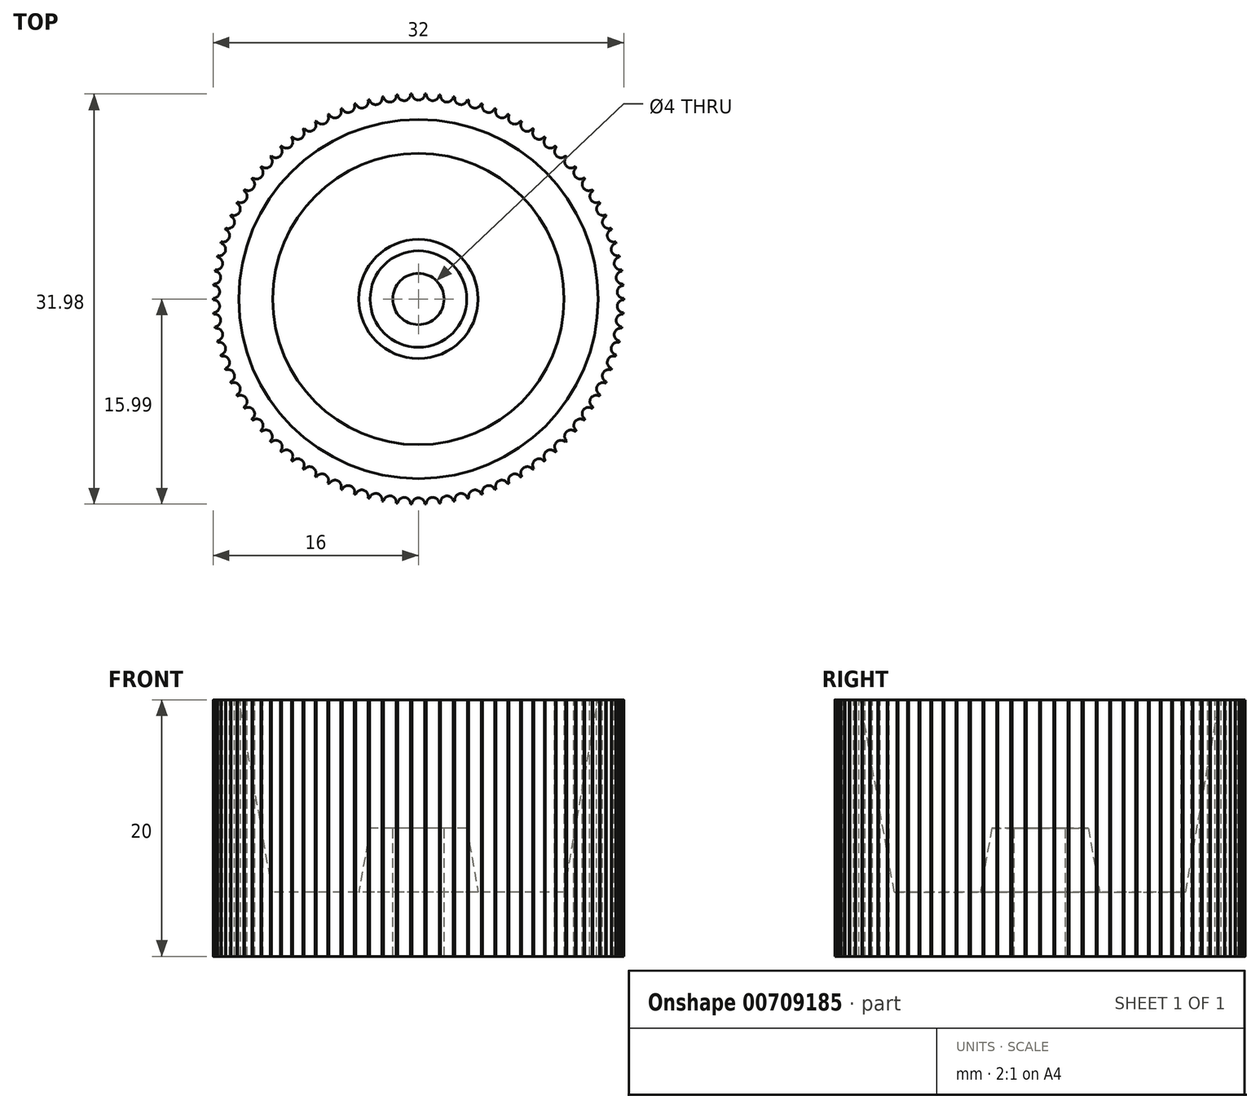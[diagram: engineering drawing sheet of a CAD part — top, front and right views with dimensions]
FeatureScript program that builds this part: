
annotation { "Feature Type Name" : "Feature", "Feature Type Description" : "" }
export const myFeature = defineFeature(function(context is Context, id is Id, definition is map)
    precondition{}
    {
        {
            var Q0;
            Q0=qCreatedBy(makeId("Top.planeOp"),FACE);
            var sketch = newSketch(context, id + "F0", { "sketchPlane" : qUnion([Q0])});
            skCircle(sketch, "E0", {"center": v(0, 0) * mm, "radius": 16 * mm});
            skCircle(sketch, "E1", {"center": v(0, 0) * mm, "radius": 14 * mm});
            skCircle(sketch, "E2", {"center": v(0, 0) * mm, "radius": 2 * mm});
            skCircle(sketch, "E3", {"center": v(0, 0) * mm, "radius": 6 * mm});
            skCircle(sketch, "E4", {"center": v(0, 16) * mm, "radius": 0.5 * mm});
            skSolve(sketch);
        }
        {
            var Q0;
            Q0=makeQuery(id+"F0.imprint","IMPRINT",FACE,{"disambiguationData":[TD([[makeQuery(id+"F0.imprint","IMPRINT",EDGE,{"derivedFrom":sQuery(id+"F0.wireOp",EDGE,"E0")}),1.0]])]});
            var Q1;
            Q1=makeQuery(id+"F0.imprint","IMPRINT",FACE,{"disambiguationData":[TD([[makeQuery(id+"F0.imprint","IMPRINT",EDGE,{"derivedFrom":sQuery(id+"F0.wireOp",EDGE,"E1")}),1.0]])]});
            var Q2;
            Q2=makeQuery(id+"F0.imprint","IMPRINT",FACE,{"disambiguationData":[TD([[makeQuery(id+"F0.imprint","IMPRINT",EDGE,{"derivedFrom":sQuery(id+"F0.wireOp",EDGE,"E2")}),-1.0]])]});
            var Q3;
            Q3=makeQuery(id+"F0.imprint","IMPRINT",FACE,{"disambiguationData":[TD([[makeQuery(id+"F0.imprint","IMPRINT",EDGE,{"derivedFrom":sQuery(id+"F0.wireOp",EDGE,"E1")}),-1.0]])]});
            extrude(context, id + "F1", {"entities" : qUnion([Q0, Q1, Q2, Q3]), "oppositeDirection" : true, "depth" : 20 * mm, "offsetDistance" : 25 * mm});
        }
        {
            var Q0;
            Q0=makeQuery(id+"F0.imprint","IMPRINT",FACE,{"disambiguationData":[TD([[makeQuery(id+"F0.imprint","IMPRINT",EDGE,{"derivedFrom":sQuery(id+"F0.wireOp",EDGE,"E1")}),1.0]])]});
            var Q1;
            Q1=makeQuery(id+"F0.imprint","IMPRINT",FACE,{"disambiguationData":[TD([[makeQuery(id+"F0.imprint","IMPRINT",EDGE,{"derivedFrom":sQuery(id+"F0.wireOp",EDGE,"E2")}),-1.0]])]});
            extrude(context, id + "F2", {"entities" : qUnion([Q0, Q1]), "operationType" : NewBodyOperationType.REMOVE, "oppositeDirection" : true, "depth" : 15 * mm, "offsetDistance" : 25 * mm, "hasDraft" : true, "draftAngle" : 10 * degree, "draftPullDirection" : true});
        }
        {
            var Q0;
            Q0=makeQuery(id+"F0.imprint","IMPRINT",FACE,{"disambiguationData":[TD([[makeQuery(id+"F0.imprint","IMPRINT",EDGE,{"derivedFrom":sQuery(id+"F0.wireOp",EDGE,"E2")}),-1.0]])]});
            extrude(context, id + "F3", {"entities" : qUnion([Q0]), "operationType" : NewBodyOperationType.REMOVE, "oppositeDirection" : true, "depth" : 10 * mm, "offsetDistance" : 25 * mm});
        }
        {
            var Q0;
            {var subQ0=sQuery(id+"F0.wireOp",EDGE,"E4");var subQ1=sQuery(id+"F0.wireOp",EDGE,"E0");var subQ2=makeQuery(id+"F0.imprint","INTERSECT",VERTEX,{"disambiguationData":[OD(0.0)],"derivedFrom":[subQ1,subQ0]});Q0=makeQuery(id+"F0.imprint","IMPRINT",FACE,{"disambiguationData":[TD([[makeQuery(id+"F0.imprint","IMPRINT",EDGE,{"disambiguationData":[TD([[subQ2,1.0]])],"derivedFrom":subQ1}),1.0]])]});}
            var Q1;
            {var subQ0=sQuery(id+"F0.wireOp",EDGE,"E4");var subQ1=sQuery(id+"F0.wireOp",EDGE,"E0");var subQ2=makeQuery(id+"F0.imprint","INTERSECT",VERTEX,{"disambiguationData":[OD(0.0)],"derivedFrom":[subQ1,subQ0]});Q1=makeQuery(id+"F0.imprint","IMPRINT",FACE,{"disambiguationData":[TD([[makeQuery(id+"F0.imprint","IMPRINT",EDGE,{"disambiguationData":[TD([[subQ2,1.0]])],"derivedFrom":subQ1}),-1.0]])]});}
            extrude(context, id + "F4", {"entities" : qUnion([Q0, Q1]), "oppositeDirection" : true, "depth" : 21 * mm, "offsetDistance" : 25 * mm, "hasSecondDirection" : true, "secondDirectionOppositeDirection" : false, "secondDirectionDepth" : 1 * mm});
        }
        {
            var Q0;
            Q0=qCreatedBy(makeId("Right.planeOp"),FACE);
            var sketch = newSketch(context, id + "F5", { "sketchPlane" : qUnion([Q0])});
            skLineSegment(sketch, "E5", {"start": v(0, 31.23) * mm, "end": v(0, -46.92) * mm});
            skSolve(sketch);
        }
        {
            var Q0;
            Q0=makeQuery(id+"F4.opExtrude","SWEPT_BODY",BODY,{"disambiguationData":[OSD([sQuery(id+"F0.wireOp",EDGE,"E4")])]});
            var Q1;
            Q1=sQuery(id+"F5.wireOp",EDGE,"E5");
            circularPattern(context, id + "F6", {"operationType" : NewBodyOperationType.REMOVE, "entities" : qUnion([Q0]), "axis" : qUnion([Q1]), "angle" : 360 * degree, "instanceCount" : 90, "equalSpace" : true});
        }
    });
